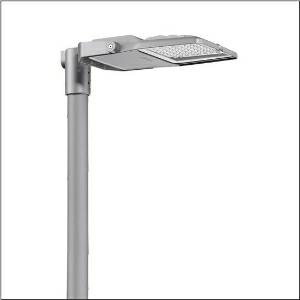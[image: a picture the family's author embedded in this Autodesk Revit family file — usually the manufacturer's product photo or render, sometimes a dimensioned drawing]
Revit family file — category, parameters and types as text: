
# Revit family: floodlight_fl_21_iq_mini___pl61_5xa7771d2c3a_41a8
name_source: partatom
category: Lighting Fixtures
units: mm (PartAtom-declared; Revit-internal decimal feet)

## family parameters
Cut with Voids When Loaded = No
Host = Face
Light Source = No
Part Type = Normal
Room Calculation Point = No
Round Connector Dimension = Use Diameter
Shared = No

## types (1)
- --- (1 x LED, 17500 lm, 143 W, 3000K)
    Apparent Load = 143 VA
    CIE Flux Codes = 33 65 98 100 100
    Color Rendering = 70
    Color Temperature = 3000K
    Default Elevation = 1800 mm
    Description = Floodlight FL 21 iQ mini, floodlight, primary light control with lens, of PMMA, primary optical cover: protective disc, of toughened safety glass, transparent, light distribution: PL61, light emission: direct distribution, installation type: surface-mounted, LED, High Power LED, rated luminous flux: 17.500lm, luminous efficacy: 122lm/W, light colour: 730, colour temperature: 3000K, control gear: iQ Comfort/DALI, control: Auto-Match, Temp-Guard, Lumen-Switch, Night-Set, Smart-Wire, Light-Fading, Desk-Remote (wireless, voltage-free reading and setting of iQ features in the workshop via application-optimized NFC function/RFID function), optimised constant luminous flux control (CLO 2.0), with terminal, 6-pole, mains connection: 220..240V, AC, 50/60Hz, start of lifetime: 143W, end of service life: 152W, reduction: 61W, luminaire housing, of diecast aluminium, powder-coated, Siteco® metallic grey (DB 702S), corrosivity category C5 mid according to DIN EN ISO 12944, suitable for swimming pools, chlorine-resistant, sealing non-destructively replaceable, please order mast flange separately, mast bracket, of steel, galvanised, powder-coated, Siteco® metallic grey (DB 702S), protection rating (complete): IP66, insulation class (complete): insulation class II (safety insulation), certification: CE, ENEC, VDE, protection symbol: D, impact resistance: IK08, permissible operating ambient temperature: -40..+40°C, permissible operating ambient temperature for outdoor applications: -40..+50°C, standard: DIN EN 12944, LABS conformity tested according to VDMA 24364:2018-05, packaging unit: 1 piece

Light Distribution: PL61
    Height = 70 mm
    Lamp = 1 x LED
    Lamp Light Flux = 17500 lm
    Lamp Power = 143 W
    Lamp count = 1
    Length = 485 mm
    Luminous efficacy = 122 lm/W
    Manufacturer = Siteco
    ModVariant = No
    Model = 5XA7771D2C3A
    Number of Poles = 1
    OnlyDefault = Yes
    Power Factor = 1
    Product Name = Floodlight FL 21 iQ mini | PL61
    Product group = floodlight | pylon annexe
    ProductGroupID = 6201
    Protection Class = Protection class II
    Protection Degree = IP 66
    RLX_Detail_Level = 1
    RLX_Emergency_Light_Flux = 0 lm
    RLX_Emergency_Type = 0
    RLX_Emergency_Type_DB = No
    RlxData = <blob elided: 101669 chars, md5=40336557>
    Socket = socket
    Standby Power = 0 W
    System Light Flux = 17500 lm
    System Power = 143 W
    Type Comments = factory setting: luminous flux: 100 % | dim-lin: 254 | 730 mA
    Type Image = l_1007125.jpg
    URL = http://relux.com
    VarID = @adj_194191
    Voltage = 0 V
    Weight = 0.00 kg
    Width = 337 mm

## geometry (parser evidence)
native form markers: Blend x4, Sweep x13
no freeform markers — native parametric forms only
